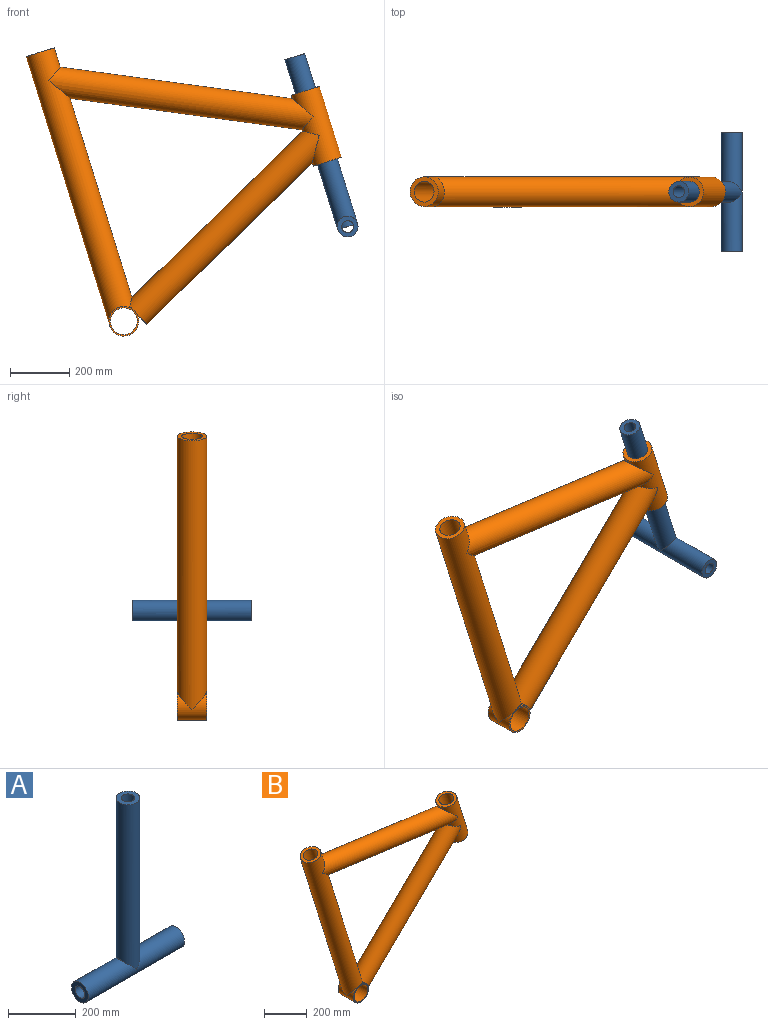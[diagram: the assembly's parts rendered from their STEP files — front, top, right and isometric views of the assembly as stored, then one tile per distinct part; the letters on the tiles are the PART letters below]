
ASSEMBLY  parts=2 mates=1
PART A: 15 faces, bbox 400x70x635 mm
  f0: cylinder r=20mm len=571.28mm, axis (0,0,-1), area 71384.5mm2, adj f2,f10
  f1: cylinder r=35mm len=600mm, axis (0,0,-1), area 127046.9mm2, adj f2,f5
  f2: plane 70x70mm, normal (0,0,1), area 2591.8mm2, adj f0,f1
  f3: plane 70x70mm, normal (-1,0,0), area 2591.8mm2, adj f5,f6
  f4: plane 70x70mm, normal (1,0,0), area 2591.8mm2, adj f5,f6
  f5: cylinder r=35mm len=400mm, axis (-1,0,0), area 83064.6mm2, adj f1,f3,f4
  f6: cylinder r=20mm len=400mm, axis (-1,0,0), area 46251.9mm2, adj f3,f4,f7,f8,f12,f13
  f7: plane 40x35mm, normal (0,0,-1), area 691.2mm2, adj f6,f8,f9
  f8: cylinder r=35mm len=40mm, axis (0,0,-1), area 657.8mm2, adj f6,f7
  f9: cylinder r=20mm len=40mm, axis (0,0,-1), area 800mm2, adj f7,f11
  f10: cylinder r=35mm len=40mm, axis (-1,0,0), area 1314.8mm2, adj f0
  f11: cylinder r=20mm len=40.14mm, axis (-1,0,0), area 1600mm2, adj f9,f14
  f12: plane 40x35mm, normal (0,0,-1), area 691.2mm2, adj f6,f13,f14
  f13: cylinder r=35mm len=40mm, axis (0,0,-1), area 657.8mm2, adj f6,f12
  f14: cylinder r=20mm len=40mm, axis (0,0,-1), area 800mm2, adj f11,f12
PART B: 31 faces, bbox 1064.3x100x972 mm
  f0: cylinder r=50mm len=42.12mm, axis (0.72,0,0.7), area 274mm2, adj f1,f17,f27
  f1: cylinder r=35mm len=893.81mm, axis (-0.3,0,0.95), area 198846.3mm2, adj f0,f9,f17,f18,f25,f27
  f2: cylinder r=50mm len=936.82mm, axis (-0.3,0,0.95), area 274107.4mm2, adj f5,f7,f8,f9,f10,f19,f22,f24
  f3: cylinder r=50mm len=58.6mm, axis (-0.3,0,0.95), area 1852.2mm2, adj f4,f24
  f4: cylinder r=35mm len=639.48mm, axis (0.72,0,0.7), area 177758.1mm2, adj f3,f6,f16,f24
  f5: cylinder r=50mm len=685.99mm, axis (0.72,0,0.7), area 257711.5mm2, adj f2,f6,f7,f8,f13,f19,f22
  f6: plane 100x35.78mm, normal (-0.72,0,-0.7), area 2002.8mm2, adj f4,f5,f24
  f7: plane 12.14x7.51mm, normal (-0.72,0,-0.7), area 66mm2, adj f2,f5,f22
  f8: plane 12.14x7.51mm, normal (-0.72,0,-0.7), area 66mm2, adj f2,f5,f19
  f9: plane 100x95.49mm, normal (-0.3,0,0.95), area 4005.5mm2, adj f1,f2
  f10: cylinder r=50mm len=905.2mm, axis (0.99,0,-0.13), area 260671.7mm2, adj f2,f13
  f11: plane 100x95.49mm, normal (-0.3,0,0.95), area 4005.5mm2, adj f13,f26
  f12: plane 100x95.49mm, normal (0.3,0,-0.95), area 4005.5mm2, adj f13,f26
  f13: cylinder r=50mm len=268.42mm, axis (-0.3,0,0.95), area 56278.5mm2, adj f5,f10,f11,f12,f14,f15
  f14: cylinder r=50mm len=0.15mm, axis (0.99,0,-0.13), area 0mm2, adj f13
  f15: cylinder r=50mm len=0.15mm, axis (0.99,0,-0.13), area 0mm2, adj f13
  f16: cylinder r=50mm len=79.28mm, axis (-0.3,0,0.95), area 4649.5mm2, adj f4
  f17: plane 42.12x11.89mm, normal (-0.72,0,-0.7), area 504.3mm2, adj f0,f1,f18
  f18: cylinder r=35mm len=20.99mm, axis (0.72,0,0.7), area 37.3mm2, adj f1,f17
  f19: cylinder r=50mm len=57.68mm, axis (0,1,0), area 304.4mm2, adj f2,f5,f8,f20
  f20: plane 100x100mm, normal (0,1,0), area 1492.3mm2, adj f19,f23,f24
  f21: plane 100x100mm, normal (0,-1,0), area 1492.3mm2, adj f22,f23,f24
  f22: cylinder r=50mm len=57.68mm, axis (0,1,0), area 304.4mm2, adj f2,f5,f7,f21
  f23: cylinder r=45mm len=100mm, axis (0,1,0), area 28274.3mm2, adj f20,f21
  f24: cylinder r=50mm len=100mm, axis (0,1,0), area 20095.5mm2, adj f2,f3,f4,f6,f20,f21
  f25: cylinder r=50mm len=70mm, axis (0,1,0), area 4144.2mm2, adj f1
  f26: cylinder r=35mm len=259.51mm, axis (-0.3,0,0.95), area 54977.9mm2, adj f11,f12
  f27: plane 15.56x2.12mm, normal (-0.3,0,0.95), area 23mm2, adj f0,f1
  f28: cylinder r=50mm len=78.01mm, axis (-0.3,0,0.95), area 4571.1mm2, adj f30
  f29: cylinder r=50mm len=78.01mm, axis (-0.3,0,0.95), area 4570.8mm2, adj f30
  f30: cylinder r=35mm len=830.47mm, axis (0.99,0,-0.13), area 176976.6mm2, adj f28,f29
PLACE A rot(axis=(-0.15,-0.15,0.98),91.3deg) t=(754.75,0,319.3)mm
PLACE B at identity fixed
MATE slider A.f0 <-> B.f13  axis (-0.3,0,0.95) through (576.5,0,892.21)mm
